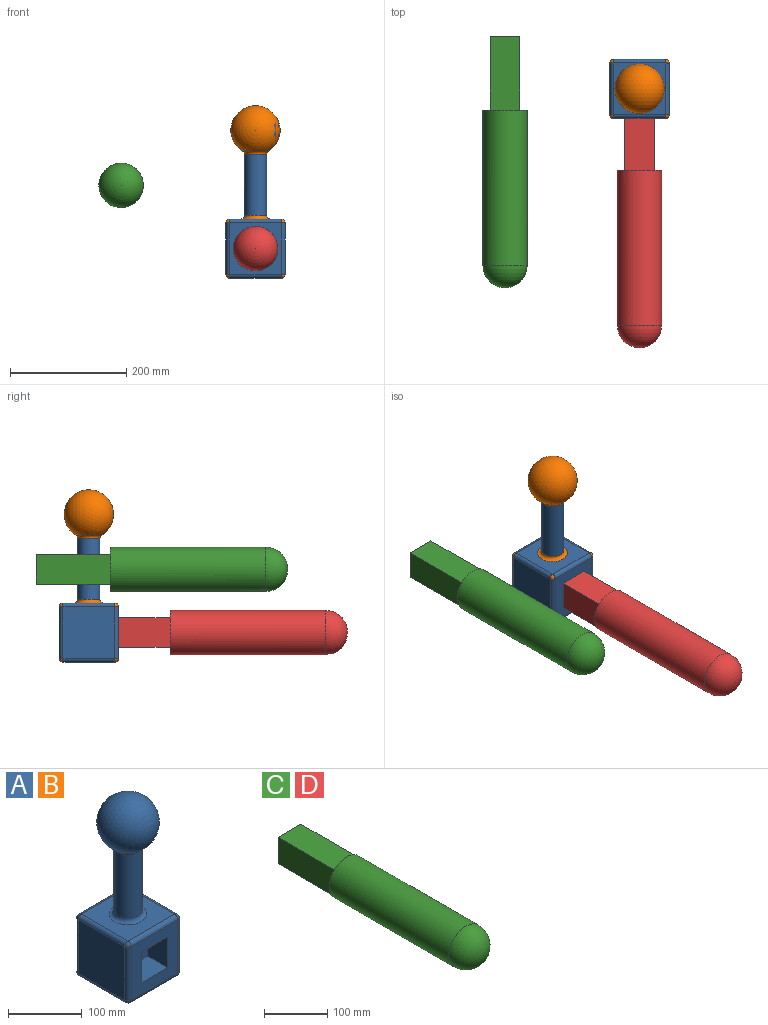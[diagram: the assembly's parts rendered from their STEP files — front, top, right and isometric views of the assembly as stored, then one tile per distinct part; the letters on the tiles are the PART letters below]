
ASSEMBLY  parts=4 mates=1
PART A: 37 faces, bbox 101.6x101.6x296.3 mm
  f0: plane 88.9x88.9mm, normal (0,-1,0), area 5322.6mm2, adj f8,f9,f10,f11,f14,f16,f19,f23
  f1: cylinder r=19.05mm len=104.55mm, axis (0,0,-1), area 12514.1mm2, adj f20,f34
  f2: plane 88.9x88.9mm, normal (-1,0,0), area 7903.2mm2, adj f17,f19,f25,f29
  f3: plane 88.9x88.9mm, normal (1,0,0), area 7903.2mm2, adj f13,f16,f21,f30
  f4: plane 88.9x88.9mm, normal (0,1,0), area 7903.2mm2, adj f26,f29,f30,f33
  f5: plane 88.9x88.9mm, normal (0,0,1), area 5876.4mm2, adj f13,f14,f17,f20,f33
  f6: plane 88.9x88.9mm, normal (0,0,-1), area 7903.2mm2, adj f21,f23,f25,f26
  f7: sphere r=42.31mm, area 20837.3mm2, adj f34
  f8: plane 50.8x38.1mm, normal (-1,0,0), area 1935.5mm2, adj f0,f9,f11,f12
  f9: plane 50.8x38.1mm, normal (0,0,-1), area 1935.5mm2, adj f0,f8,f10,f12
  f10: plane 50.8x38.1mm, normal (1,0,0), area 1935.5mm2, adj f0,f9,f11,f12
  f11: plane 50.8x38.1mm, normal (0,0,1), area 1935.5mm2, adj f0,f8,f10,f12
  f12: plane 50.8x50.8mm, normal (0,-1,0), area 2580.6mm2, adj f8,f9,f10,f11
  f13: cylinder r=6.35mm len=88.9mm, axis (0,-1,0), area 886.7mm2, adj f3,f5,f15,f32
  f14: cylinder r=6.35mm len=88.9mm, axis (-1,0,0), area 886.7mm2, adj f0,f5,f15,f18
  f15: sphere r=6.35mm, area 63.3mm2, adj f13,f14,f16
  f16: cylinder r=6.35mm len=88.9mm, axis (0,0,1), area 886.7mm2, adj f0,f3,f15,f22
  f17: cylinder r=6.35mm len=88.9mm, axis (0,1,0), area 886.7mm2, adj f2,f5,f18,f31
  f18: sphere r=6.35mm, area 63.3mm2, adj f14,f17,f19
  f19: cylinder r=6.35mm len=88.9mm, axis (0,0,-1), area 886.7mm2, adj f0,f2,f18,f24
  f20: torus R=25.4mm, axis (0,0,1), area 1338.5mm2, adj f1,f5
  f21: cylinder r=6.35mm len=88.9mm, axis (0,1,0), area 886.7mm2, adj f3,f6,f22,f28
  f22: sphere r=6.35mm, area 63.3mm2, adj f16,f21,f23
  f23: cylinder r=6.35mm len=88.9mm, axis (1,0,0), area 886.7mm2, adj f0,f6,f22,f24
  f24: sphere r=6.35mm, area 63.3mm2, adj f19,f23,f25
  f25: cylinder r=6.35mm len=88.9mm, axis (0,-1,0), area 886.7mm2, adj f2,f6,f24,f27
  f26: cylinder r=6.35mm len=88.9mm, axis (-1,0,0), area 886.7mm2, adj f4,f6,f27,f28
  f27: sphere r=6.35mm, area 63.3mm2, adj f25,f26,f29
  f28: sphere r=6.35mm, area 63.3mm2, adj f21,f26,f30
  f29: cylinder r=6.35mm len=88.9mm, axis (0,0,1), area 886.7mm2, adj f2,f4,f27,f31
  f30: cylinder r=6.35mm len=88.9mm, axis (0,0,-1), area 886.7mm2, adj f3,f4,f28,f32
  f31: sphere r=6.35mm, area 63.3mm2, adj f17,f29,f33
  f32: sphere r=6.35mm, area 63.3mm2, adj f13,f30,f33
  f33: cylinder r=6.35mm len=88.9mm, axis (1,0,0), area 886.7mm2, adj f4,f5,f31,f32
  f34: torus R=25.4mm, axis (0,0,1), area 819.2mm2, adj f1,f7
  f35: sphere r=19.05mm, area 2280.2mm2, adj f36
  f36: plane 38.1x38.1mm, normal (0,0,1), area 1140.1mm2, adj f35
PART B: same geometry as A
PART C: 8 faces, bbox 76.2x431.8x76.2 mm
  f0: plane 127x50.8mm, normal (-1,0,0), area 6451.6mm2, adj f1,f3,f4,f5
  f1: plane 127x50.8mm, normal (0,0,-1), area 6451.6mm2, adj f0,f2,f4,f5
  f2: plane 127x50.8mm, normal (1,0,0), area 6451.6mm2, adj f1,f3,f4,f5
  f3: plane 127x50.8mm, normal (0,0,1), area 6451.6mm2, adj f0,f2,f4,f5
  f4: plane 50.8x50.8mm, normal (0,1,0), area 2580.6mm2, adj f0,f1,f2,f3
  f5: plane 76.2x76.2mm, normal (0,1,0), area 1979.7mm2, adj f0,f1,f2,f3,f6
  f6: cylinder r=38.1mm len=266.7mm, axis (0,1,0), area 63845.1mm2, adj f5,f7
  f7: sphere r=38.1mm, area 9120.7mm2, adj f6
PART D: same geometry as C
PLACE A t=(-28.57,41.55,-61.09)mm fixed
PLACE B t=(-28.57,41.55,-61.09)mm
PLACE C t=(-259.5,131.69,98.42)mm
PLACE D t=(-28.57,28.85,-10.29)mm
MATE fastened D.f6 <-> A.f12  axis (0,1,0) through (-28.57,28.85,-10.29)mm
